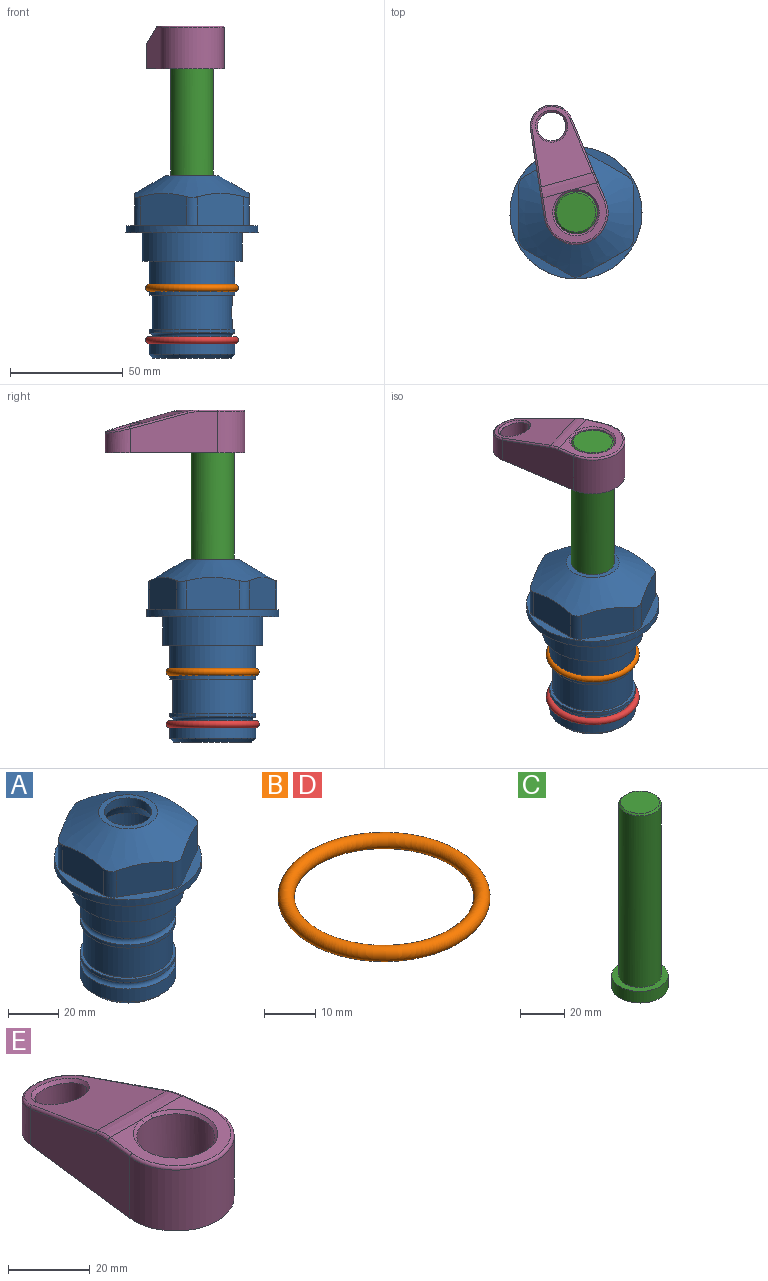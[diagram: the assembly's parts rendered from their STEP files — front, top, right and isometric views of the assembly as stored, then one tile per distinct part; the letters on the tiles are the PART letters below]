
ASSEMBLY  parts=5 mates=4
PART A: 36 faces, bbox 58.7x58.7x81 mm
  f0: cylinder r=17.78mm len=35.56mm, axis (0,0,1), area 1670.8mm2, adj f23,f24,f31
  f1: cylinder r=19.05mm len=38.1mm, axis (0,0,1), area 1191.9mm2, adj f26,f27,f30
  f2: plane 58.66x58.66mm, normal (0,0,-1), area 1150.6mm2, adj f3,f28
  f3: cylinder r=29.33mm len=58.66mm, axis (0,0,-1), area 585.1mm2, adj f2,f4
  f4: plane 58.66x58.66mm, normal (0,0,1), area 475.9mm2, adj f3,f5,f6,f7,f8,f9,f10,f11
  f5: plane 20.32x14.34mm, normal (-0.5,0.87,0), area 324.4mm2, adj f4,f15,f16,f17
  f6: plane 20.32x14.34mm, normal (0.5,0.87,0), area 324.4mm2, adj f4,f14,f15,f17
  f7: plane 23.48x14.34mm, normal (1,0,0), area 324.4mm2, adj f4,f13,f14,f17
  f8: plane 20.32x14.34mm, normal (0.5,-0.87,0), area 324.4mm2, adj f4,f12,f13,f17
  f9: plane 20.32x14.34mm, normal (-0.5,-0.87,0), area 324.4mm2, adj f4,f11,f12,f17
  f10: plane 23.48x14.34mm, normal (-1,0,0), area 324.4mm2, adj f4,f11,f16,f17
  f11: cylinder r=5.08mm len=12.85mm, axis (0,0,-1), area 67.2mm2, adj f4,f9,f10,f17
  f12: cylinder r=5.08mm len=12.85mm, axis (0,0,-1), area 67.2mm2, adj f4,f8,f9,f17
  f13: cylinder r=5.08mm len=12.85mm, axis (0,0,-1), area 67.2mm2, adj f4,f7,f8,f17
  f14: cylinder r=5.08mm len=12.85mm, axis (0,0,-1), area 67.2mm2, adj f4,f6,f7,f17
  f15: cylinder r=5.08mm len=12.85mm, axis (0,0,-1), area 67.2mm2, adj f4,f5,f6,f17
  f16: cylinder r=5.08mm len=12.85mm, axis (0,0,-1), area 67.2mm2, adj f4,f5,f10,f17
  f17: cone r=11.73mm half-angle=60deg, axis (0,0,-1), area 2071.8mm2, adj f5,f6,f7,f8,f9,f10,f11,f12
  f18: plane 23.46x23.46mm, normal (0,0,1), area 147.4mm2, adj f17,f35
  f19: plane 34.93x34.93mm, normal (0,0,-1), area 958mm2, adj f29
  f20: cylinder r=19.05mm len=38.1mm, axis (0,0,1), area 760.1mm2, adj f21,f29
  f21: torus R=19.05mm, axis (0,0,1), area 565.3mm2, adj f20,f22
  f22: cylinder r=19.05mm len=38.1mm, axis (0,0,1), area 190mm2, adj f21,f23
  f23: plane 38.1x38.1mm, normal (0,0,1), area 146.9mm2, adj f0,f22
  f24: plane 38.1x38.1mm, normal (0,0,-1), area 146.9mm2, adj f0,f25
  f25: cylinder r=19.05mm len=38.1mm, axis (0,0,1), area 190mm2, adj f24,f26
  f26: torus R=19.05mm, axis (0,0,1), area 565.3mm2, adj f1,f25
  f27: plane 44.45x44.45mm, normal (0,0,-1), area 411.7mm2, adj f1,f28
  f28: cylinder r=22.23mm len=44.45mm, axis (0,0,1), area 1773.5mm2, adj f2,f27
  f29: cone r=19.05mm half-angle=45deg, axis (0,0,1), area 257.5mm2, adj f19,f20
  f30: cylinder r=3.17mm len=6.75mm, axis (-1,0,0), area 128mm2, adj f1,f33
  f31: cylinder r=3.17mm len=6.35mm, axis (-1,0,0), area 102.5mm2, adj f0,f33
  f32: plane 25.4x25.4mm, normal (0,0,1), area 506.7mm2, adj f33
  f33: cylinder r=12.7mm len=66.42mm, axis (0,0,-1), area 5236.2mm2, adj f30,f31,f32,f34
  f34: cone r=9.53mm half-angle=30deg, axis (0,0,-1), area 443.4mm2, adj f33,f35
  f35: cylinder r=9.53mm len=19.05mm, axis (0,0,-1), area 240.9mm2, adj f18,f34
PART B: 1 faces, bbox 44.7x44.7x3.2 mm
  f0: torus R=19.05mm, axis (0,0,1), area 1193.9mm2
PART C: 6 faces, bbox 25.4x25.4x101.6 mm
  f0: plane 17.46x17.46mm, normal (0,0,1), area 239.5mm2, adj f5
  f1: plane 25.4x25.4mm, normal (0,0,-1), area 506.7mm2, adj f2
  f2: cylinder r=12.7mm len=25.4mm, axis (0,0,1), area 506.7mm2, adj f1,f3
  f3: plane 25.4x25.4mm, normal (0,0,1), area 221.7mm2, adj f2,f4
  f4: cylinder r=9.53mm len=94.46mm, axis (0,0,1), area 5653mm2, adj f3,f5
  f5: cone r=8.73mm half-angle=45deg, axis (0,0,-1), area 64.4mm2, adj f0,f4
PART D: same geometry as B
PART E: 31 faces, bbox 31.7x65.5x19.8 mm
  f0: plane 39.12x18.26mm, normal (0.99,0.12,0), area 612.2mm2, adj f1,f4,f7,f11,f13,f15
  f1: cylinder r=9.53mm len=18.91mm, axis (0,0,-1), area 296.1mm2, adj f0,f2,f7,f17
  f2: plane 39.12x18.26mm, normal (-0.99,0.12,0), area 612.2mm2, adj f1,f4,f7,f12,f14,f16
  f3: cylinder r=6.35mm len=12.7mm, axis (0,0,-1), area 362.4mm2, adj f7,f18
  f4: cylinder r=14.29mm len=28.58mm, axis (0,0,-1), area 882.2mm2, adj f0,f2,f7,f10
  f5: cylinder r=9.53mm len=19.05mm, axis (0,0,-1), area 1092.6mm2, adj f7,f19,f20
  f6: plane 26.99x23.69mm, normal (0,0,1), area 216.2mm2, adj f9,f10,f11,f12,f19
  f7: plane 63.5x28.58mm, normal (0,0,-1), area 661.8mm2, adj f0,f1,f2,f3,f4,f5,f22,f23
  f8: plane 33.52x23.6mm, normal (0,0.26,0.97), area 486mm2, adj f9,f15,f16,f17,f18
  f9: cylinder r=19.05mm len=24.72mm, axis (1,0,0), area 120.4mm2, adj f6,f8,f13,f14,f20
  f10: torus R=13.49mm, axis (0,0,1), area 59mm2, adj f4,f6,f11,f12
  f11: cylinder r=0.79mm len=8.67mm, axis (0.12,-0.99,0), area 10.8mm2, adj f0,f6,f10,f13
  f12: cylinder r=0.79mm len=8.67mm, axis (0.12,0.99,0), area 10.8mm2, adj f2,f6,f10,f14
  f13: bspline ~4.95x1.42mm, area 6.1mm2, adj f0,f9,f11,f15
  f14: bspline ~4.95x1.42mm, area 6.1mm2, adj f2,f9,f12,f16
  f15: cylinder r=0.79mm len=25.95mm, axis (0.12,-0.96,0.26), area 32.9mm2, adj f0,f8,f13,f17
  f16: cylinder r=0.79mm len=25.95mm, axis (0.12,0.96,-0.26), area 32.9mm2, adj f2,f8,f14,f17
  f17: bspline ~18.91x8.38mm, area 30mm2, adj f1,f8,f15,f16
  f18: bspline ~14.29x14.29mm, area 48.3mm2, adj f3,f8
  f19: cone r=9.53mm half-angle=45deg, axis (0,0,1), area 66.5mm2, adj f5,f6,f20
  f20: bspline ~3.22x0.96mm, area 3.5mm2, adj f5,f9,f19
  f21: plane 2.75x2.72mm, normal (0,0,-1), area 2.9mm2, adj f23,f25,f28
  f22: plane 23.05x15.88mm, normal (-0.99,-0.12,0), area 323.6mm2, adj f7,f25,f26,f27,f28,f29
  f23: plane 23.05x15.88mm, normal (0.99,-0.12,0), area 323.6mm2, adj f7,f21,f25,f27,f28,f30
  f24: cylinder r=9.53mm len=10.69mm, axis (0,0,-1), area 114.7mm2, adj f7,f27,f29,f30
  f25: cylinder r=12.7mm len=20.59mm, axis (0,0,-1), area 381.1mm2, adj f7,f21,f22,f23,f26,f28
  f26: plane 2.75x2.72mm, normal (0,0,-1), area 2.9mm2, adj f22,f25,f28
  f27: plane 19.72x18.37mm, normal (0,-0.26,-0.97), area 291.8mm2, adj f22,f23,f24,f28,f29,f30
  f28: cylinder r=15.88mm len=19.92mm, axis (1,0,0), area 54.8mm2, adj f21,f22,f23,f25,f26,f27
  f29: cylinder r=1.59mm len=11mm, axis (0,0,-1), area 34.7mm2, adj f7,f22,f24,f27
  f30: cylinder r=1.59mm len=11mm, axis (0,0,-1), area 34.7mm2, adj f7,f23,f24,f27
PLACE A at identity fixed
PLACE B at identity
PLACE C rot(axis=(0,0,1),15.8deg) t=(0,0,27.55)mm
PLACE D rot(axis=(1,0,0),180deg) t=(0,0,-72.2)mm
PLACE E rot(axis=(0,0,1),15.8deg) t=(0,0,28.35)mm
MATE fastened C.f2 <-> E.f4  axis (0,0,1) through (0,0,91.05)mm
MATE fastened A.f0 <-> B.f0  axis (0,0,1) through (0,0,-24.51)mm
MATE cylindrical A.f0 <-> C.f2  axis (0,0,1) through (0,0,-50.55)mm
MATE fastened A.f0 <-> D.f0  axis (0,0,1) through (0,0,-47.69)mm
